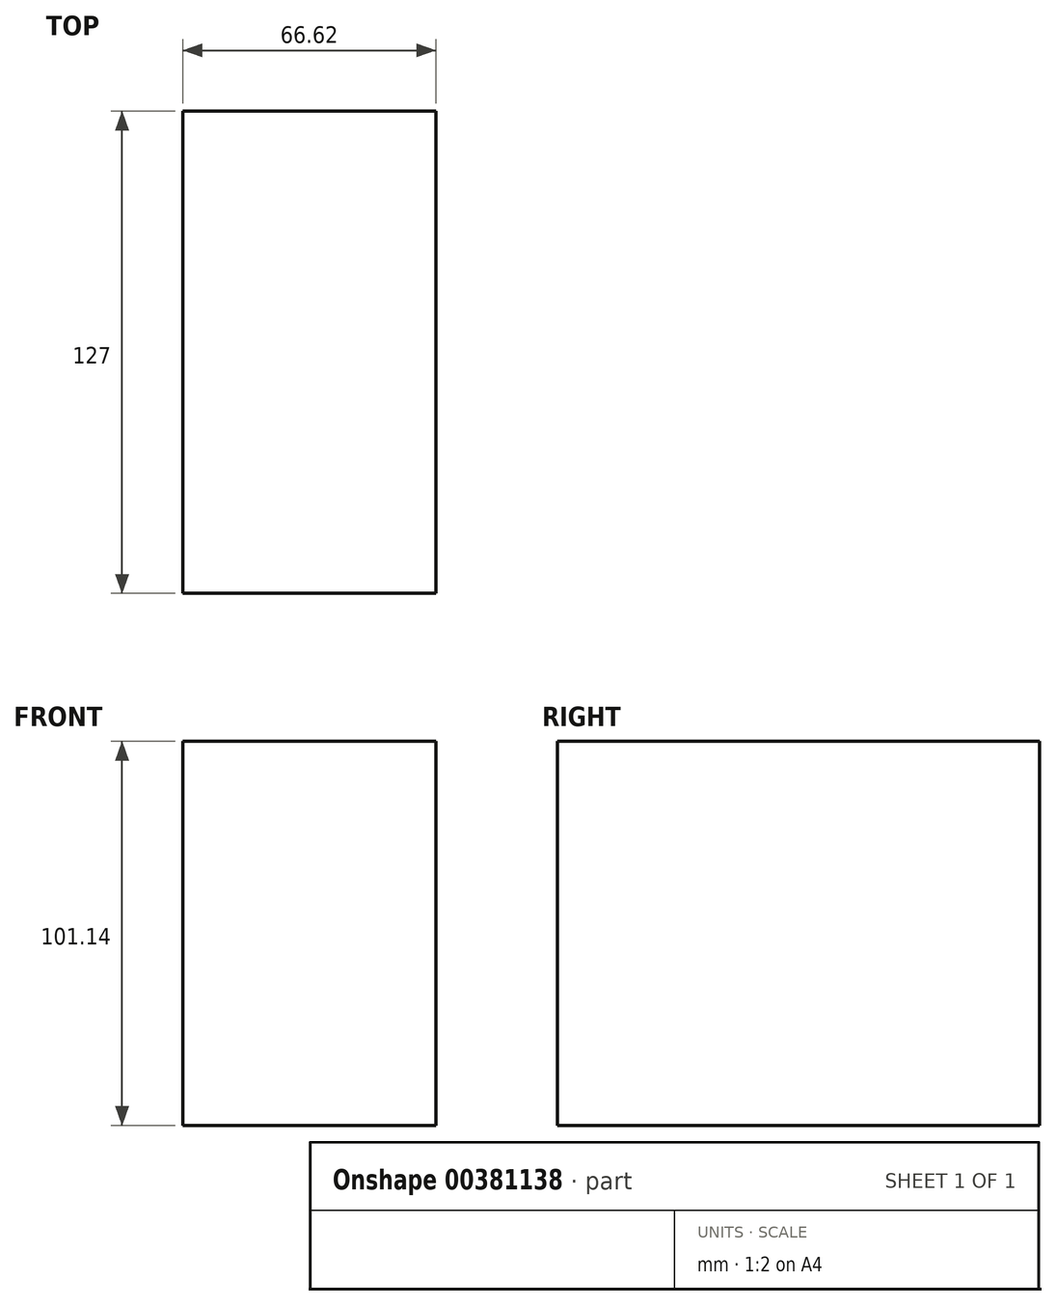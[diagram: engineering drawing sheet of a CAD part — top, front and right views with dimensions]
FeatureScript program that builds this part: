
annotation { "Feature Type Name" : "Feature", "Feature Type Description" : "" }
export const myFeature = defineFeature(function(context is Context, id is Id, definition is map)
    precondition{}
    {
        {
            var Q0;
            Q0=qCreatedBy(makeId("Front.planeOp"),FACE);
            var sketch = newSketch(context, id + "F0", { "sketchPlane" : qUnion([Q0])});
            skLineSegment(sketch, "E0.bottom", {"start": v(-34.98, 36.72) * mm, "end": v(31.64, 36.72) * mm});
            skLineSegment(sketch, "E0.top", {"start": v(-34.98, -64.42) * mm, "end": v(31.64, -64.42) * mm});
            skLineSegment(sketch, "E0.left", {"start": v(-34.98, 36.72) * mm, "end": v(-34.98, -64.42) * mm});
            skLineSegment(sketch, "E0.right", {"start": v(31.64, 36.72) * mm, "end": v(31.64, -64.42) * mm});
            skSolve(sketch);
        }
        {
            var Q0;
            Q0 = qSketchRegion(id + "F0", true);
            extrude(context, id + "F1", {"entities" : qUnion([Q0]), "depth" : 127 * mm});
        }
    });
